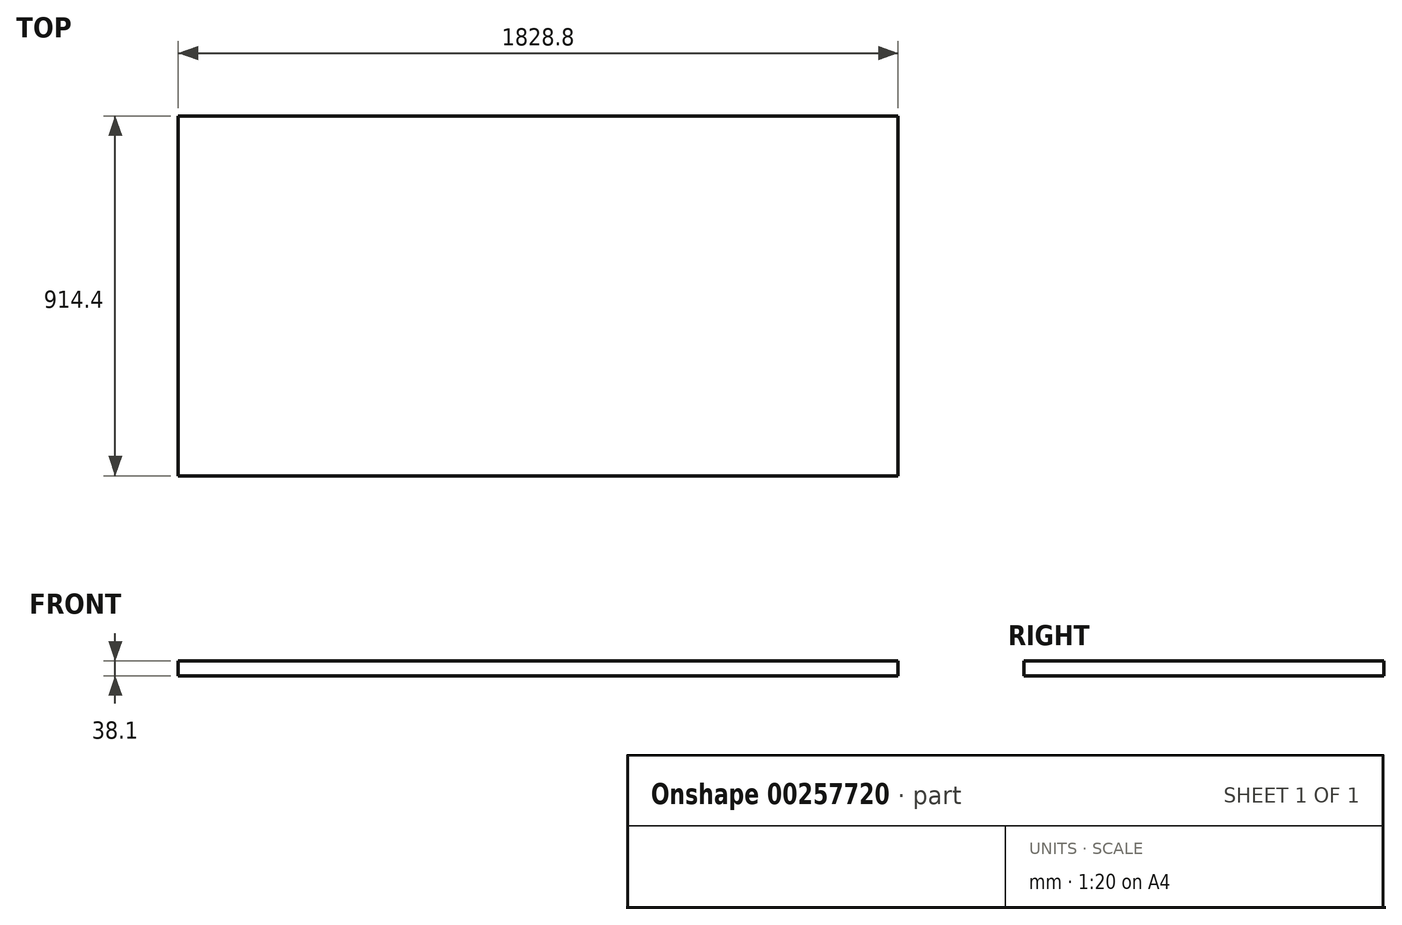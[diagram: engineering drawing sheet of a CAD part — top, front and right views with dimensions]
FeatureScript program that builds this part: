
annotation { "Feature Type Name" : "Feature", "Feature Type Description" : "" }
export const myFeature = defineFeature(function(context is Context, id is Id, definition is map)
    precondition{}
    {
        {
            var Q0;
            Q0=qCreatedBy(makeId("Top.planeOp"),FACE);
            var sketch = newSketch(context, id + "F0", { "sketchPlane" : qUnion([Q0])});
            skLineSegment(sketch, "E0.bottom", {"start": v(-914.4, -457.2) * mm, "end": v(914.4, -457.2) * mm});
            skLineSegment(sketch, "E0.top", {"start": v(-914.4, 457.2) * mm, "end": v(914.4, 457.2) * mm});
            skLineSegment(sketch, "E0.left", {"start": v(-914.4, -457.2) * mm, "end": v(-914.4, 457.2) * mm});
            skLineSegment(sketch, "E0.right", {"start": v(914.4, -457.2) * mm, "end": v(914.4, 457.2) * mm});
            skSolve(sketch);
        }
        {
            var Q0;
            Q0 = qSketchRegion(id + "F0", true);
            extrude(context, id + "F1", {"entities" : qUnion([Q0]), "endBound" : BoundingType.SYMMETRIC, "depth" : 38.1 * mm});
        }
    });
